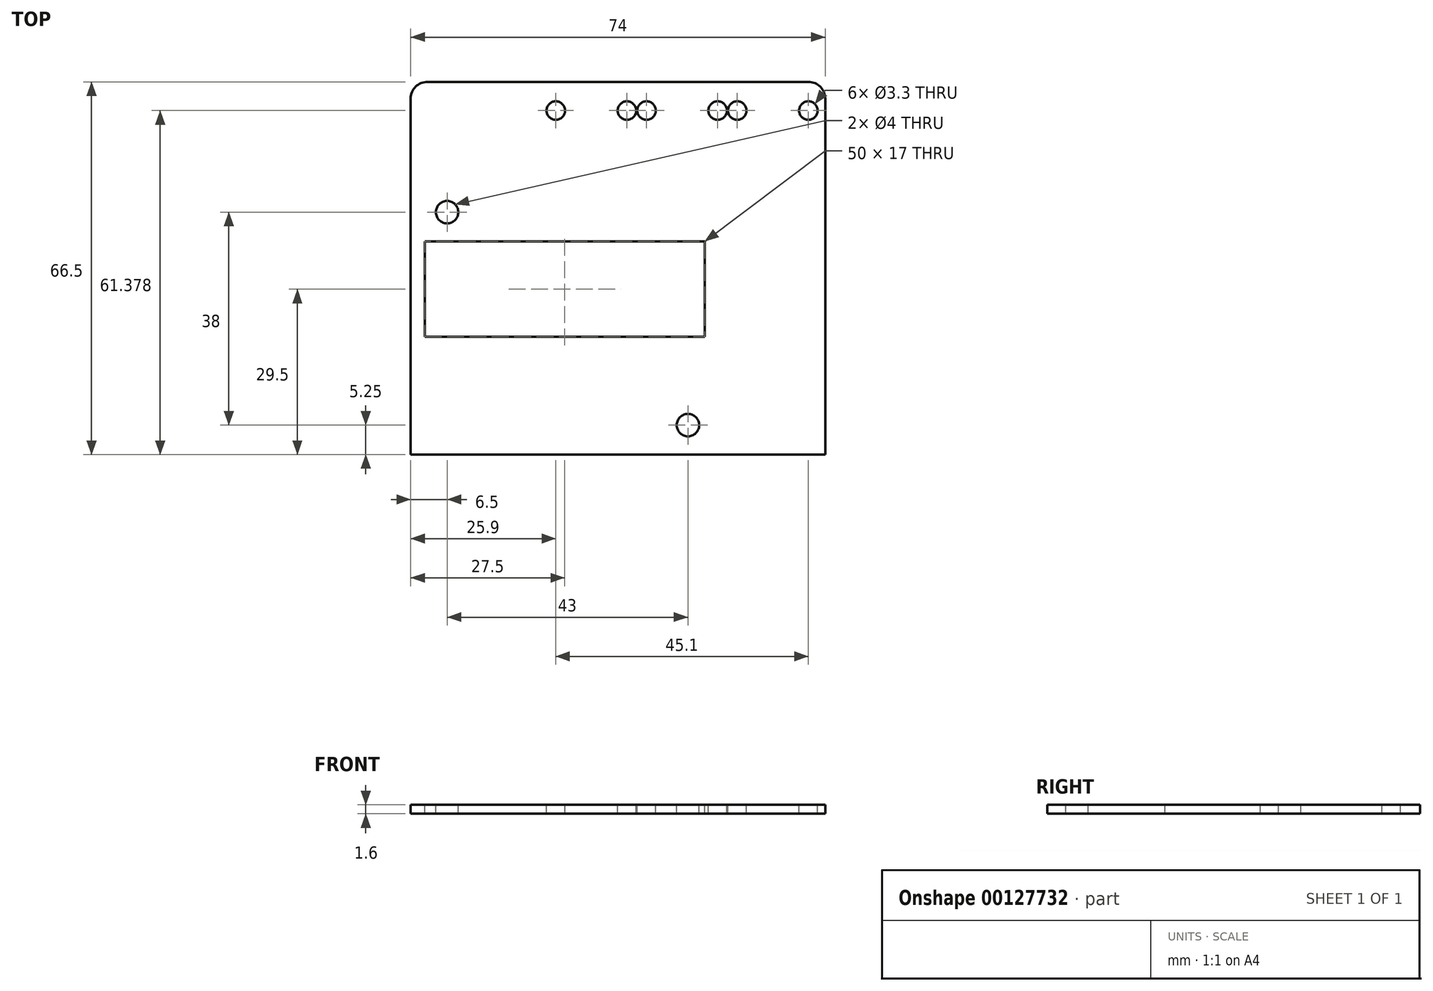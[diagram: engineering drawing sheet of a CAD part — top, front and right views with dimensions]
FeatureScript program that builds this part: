
annotation { "Feature Type Name" : "Feature", "Feature Type Description" : "" }
export const myFeature = defineFeature(function(context is Context, id is Id, definition is map)
    precondition{}
    {
        {
            var Q0;
            Q0=qCreatedBy(makeId("Top.planeOp"),FACE);
            var sketch = newSketch(context, id + "F0", { "sketchPlane" : qUnion([Q0])});
            skLineSegment(sketch, "E0.bottom", {"start": v(-27.5, 42.25) * mm, "end": v(46.5, 42.25) * mm});
            skLineSegment(sketch, "E0.top", {"start": v(-27.5, -24.25) * mm, "end": v(46.5, -24.25) * mm});
            skLineSegment(sketch, "E0.left", {"start": v(-27.5, 42.25) * mm, "end": v(-27.5, -24.25) * mm});
            skLineSegment(sketch, "E0.right", {"start": v(46.5, 42.25) * mm, "end": v(46.5, -24.25) * mm});
            skSolve(sketch);
        }
        {
            var Q0;
            Q0 = qSketchRegion(id + "F0", true);
            extrude(context, id + "F1", {"entities" : qUnion([Q0]), "depth" : 1.6 * mm});
        }
        {
            var Q0;
            Q0=makeQuery(id+"F1.opExtrude","SWEPT_EDGE",EDGE,{"disambiguationData":[OSD([sQuery(id+"F0.wireOp",EDGE,"E0.bottom"),sQuery(id+"F0.wireOp",EDGE,"E0.left")])]});
            var Q1;
            Q1=makeQuery(id+"F1.opExtrude","SWEPT_EDGE",EDGE,{"disambiguationData":[OSD([sQuery(id+"F0.wireOp",EDGE,"E0.bottom"),sQuery(id+"F0.wireOp",EDGE,"E0.right")])]});
            fillet(context, id + "F2", {"entities" : qUnion([Q0, Q1]), "radius" : 3 * mm, "tangentPropagation" : true, "allowEdgeOverflow" : false});
        }
        {
            var Q0;
            Q0=makeQuery(id+"F1.opExtrude","CAP_FACE",FACE,{"disambiguationData":[OSD([sQuery(id+"F0.wireOp",EDGE,"E0.bottom"),sQuery(id+"F0.wireOp",EDGE,"E0.top"),sQuery(id+"F0.wireOp",EDGE,"E0.left"),sQuery(id+"F0.wireOp",EDGE,"E0.right")])],"isStart":false});
            var sketch = newSketch(context, id + "F3", { "sketchPlane" : qUnion([Q0])});
            skCircle(sketch, "E1", {"center": v(-21, 19) * mm, "radius": 2 * mm});
            skCircle(sketch, "E2", {"center": v(22, -19) * mm, "radius": 2 * mm});
            skLineSegment(sketch, "E3.bottom", {"start": v(25, -3.25) * mm, "end": v(-25, -3.25) * mm});
            skLineSegment(sketch, "E3.top", {"start": v(25, 13.75) * mm, "end": v(-25, 13.75) * mm});
            skLineSegment(sketch, "E3.left", {"start": v(25, -3.25) * mm, "end": v(25, 13.75) * mm});
            skLineSegment(sketch, "E3.right", {"start": v(-25, -3.25) * mm, "end": v(-25, 13.75) * mm});
            skCircle(sketch, "E4", {"center": v(-1.6, 37.13) * mm, "radius": 1.65 * mm});
            skCircle(sketch, "E5", {"center": v(11.1, 37.13) * mm, "radius": 1.65 * mm});
            skCircle(sketch, "E6", {"center": v(14.6, 37.13) * mm, "radius": 1.65 * mm});
            skCircle(sketch, "E7", {"center": v(27.3, 37.13) * mm, "radius": 1.65 * mm});
            skCircle(sketch, "E8", {"center": v(30.8, 37.13) * mm, "radius": 1.65 * mm});
            skCircle(sketch, "E9", {"center": v(43.5, 37.13) * mm, "radius": 1.65 * mm});
            skSolve(sketch);
        }
        {
            var Q0;
            Q0 = qSketchRegion(id + "F3", true);
            extrude(context, id + "F4", {"entities" : qUnion([Q0]), "operationType" : NewBodyOperationType.REMOVE, "oppositeDirection" : true, "depth" : 25 * mm});
        }
    });
